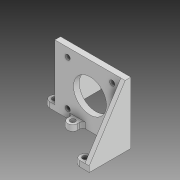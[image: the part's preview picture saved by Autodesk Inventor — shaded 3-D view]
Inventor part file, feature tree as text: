
AUTODESK INVENTOR PART (.ipt)
format: ipt  version: 2020 (Build 240168000, 168)  size: 206,336 bytes
history: native  units: mm
features: extrude x4, sketch x4, fillet x2, projected_geometry x2
ambient origin geometry x8: Origin, YZ Plane, XZ Plane, XY Plane, X Axis, Y Axis, Z Axis, Center Point
bodies: Solid1 (feature_tree)
feature tree (12):
  extrude  "Extrusion1"  Depth=4.0mm TaperAngle=0.0deg
  extrude  "Extrusion2"  Depth=4.0mm
  extrude  "Extrusion3"  Depth=4.0mm
  extrude  "Extrusion4"  Depth=3.0mm TaperAngle=0.0deg
  fillet  "Fillet1"  Radius=3.5mm
  fillet  "Fillet2"  Radius=3.5mm
  sketch  "Sketch1"  dims[d0=23.0mm d1=3.5mm d2=31.0mm d3=31.0mm d4=43.0mm d5=4.0mm d6=0.0mm]
  sketch  "Sketch2"  dims[d7=28.0mm d8=4.0mm]
  projected_geometry  "Projected Loop1"
  sketch  "Sketch3"  dims[d9=3.0mm d10=0.0mm d11=4.0mm]
  projected_geometry  "Projected Loop2"
  sketch  "Sketch4"  dims[d12=25.0mm d13=3.0mm d14=0.0mm d15=3.5mm d16=3.5mm d17=4.0mm d18=0.0mm d19=3.5mm d20=3.5mm d21=3.5mm d22=3.5mm d23=3.5mm d24=3.5mm d25=16.0mm d26=2.0mm d27=25.5mm d28=6.5mm d31=26.5mm d32=19.5mm d33=18.0mm d34=7.0mm d35=25.0mm d36=3.0mm]
